# Revit family: FEVB 2 WIDE
name_source: partatom
category: Mechanical Equipment
units: mm (PartAtom-declared; Revit-internal decimal feet)

## family parameters
Always vertical = Yes
Classification = None
Cut with Voids When Loaded = No
OmniClass Number = 23.75.00.00
OmniClass Title = Climate Control (HVAC)
Part Type = Normal
Room Calculation Point = No
Round Connector Dimension = Use Diameter
Shared = No
Work Plane-Based = No

## types (6) — shared parameters
Copper Pipes = Copper Pipe
Description = FLUID COOLERS (FEVB)
Fan001 = Yes
Fan002 = Yes
Full Load Amps (FLA) = Amps-1
Full load Amps (FLA)-2 = Amps-2
Inlet Pipe Size = 2"
Inlet Pipe Size (Radius) = 1.06 "
Manufacturer = HUSSMANN CORPORATION
Model = FEVB 2 WIDE
Outlet Pipe Size = 2"
Outlet Pipe Size (Radius) = 1"
Phase = 3
Revit Family Dates = 08/18/2023 HM
TEXT = 1 "
Type Comments = Systems
Voltage = 460 V
Voltage - 2 = 208 V

## per-type parameters (varying)
| type | Fan003 | Fan004 | Fan005 | Fan006 | Fan007 | Leg A | Leg B | Leg C | Leg D | Legs | Over all height | URL | Unit Width |
| FEVB 2 X 2 | No | No | No | No | No | No | No | No | No | 72.12 " | 41.44 " |  | 76.28 " |
| FEVB 2 X 3 | Yes | No | No | No | No | No | No | No | No | 108.12 " | 41.44 " |  | 112.68 " |
| FEVB 2 X 4 | Yes | Yes | No | No | No | Yes | No | No | No | 144.12 " | 44.1 " |  | 148 " |
| FEVB 2 X 5 | Yes | Yes | Yes | No | No | No | Yes | No | No | 180.12 " | 41.44 " |  | 184.28 " |
| FEVB 2 X 6 | Yes | Yes | Yes | Yes | No | No | No | Yes | No | 216.12 " | 41.44 " |  | 220.28 " |
| FEVB 2 X 7 | Yes | Yes | Yes | Yes | Yes | No | No | No | Yes | 252.12 " | 41.44 " | hussmann.com | 256.28 " |

## geometry (parser evidence)
native form markers: Sweep x41
no freeform markers — native parametric forms only
